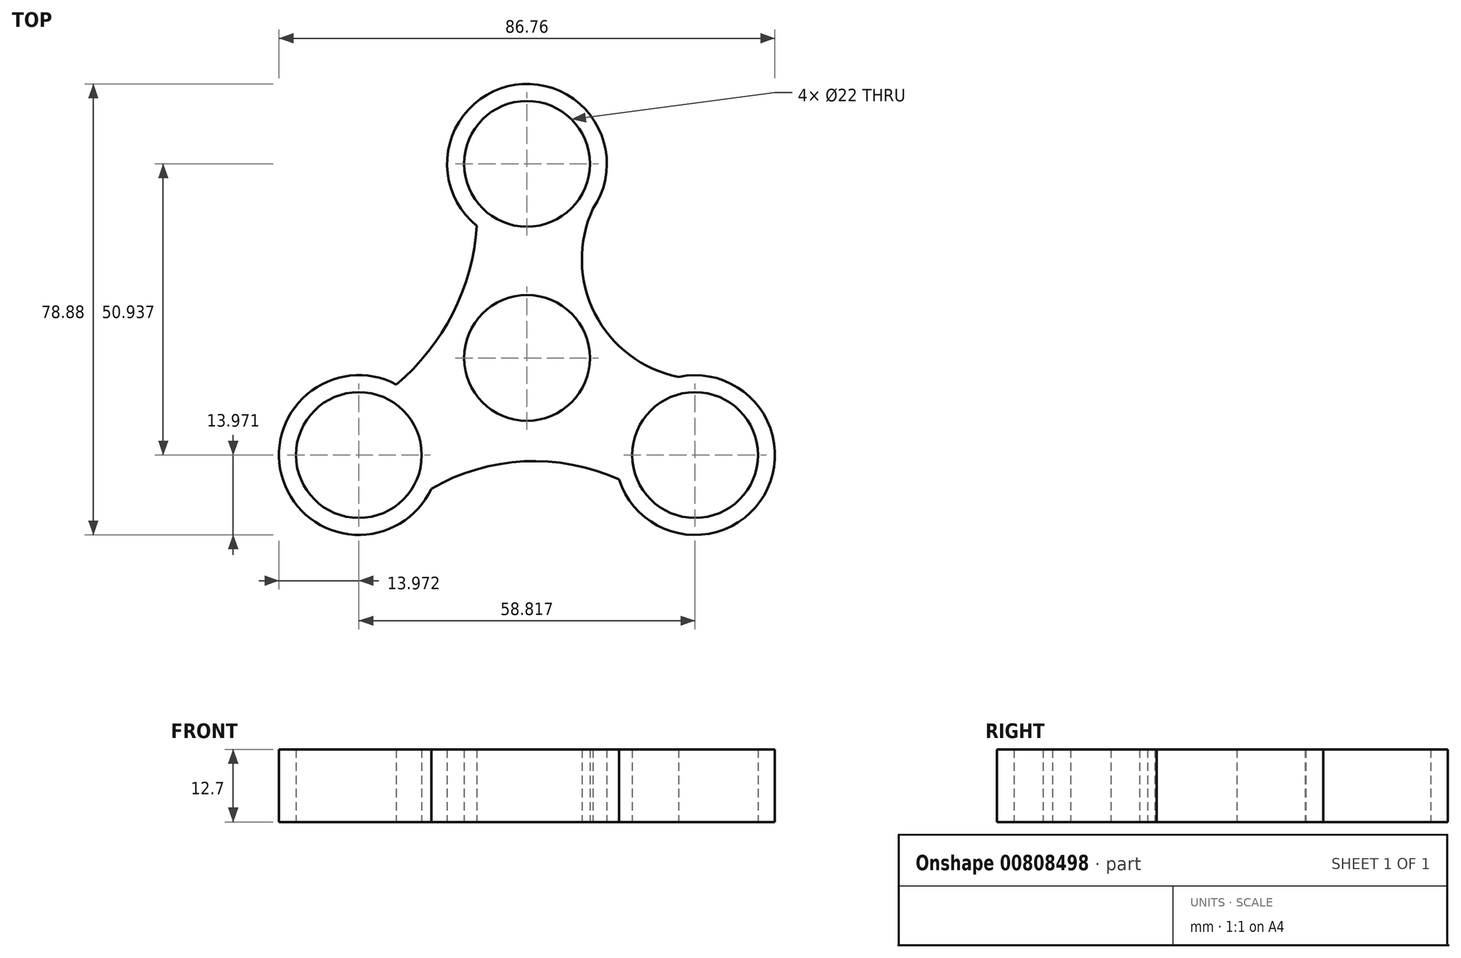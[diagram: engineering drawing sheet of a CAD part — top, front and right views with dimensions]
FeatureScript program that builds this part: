
annotation { "Feature Type Name" : "Feature", "Feature Type Description" : "" }
export const myFeature = defineFeature(function(context is Context, id is Id, definition is map)
    precondition{}
    {
        {
            var Q0;
            Q0=qCreatedBy(makeId("Top.planeOp"),FACE);
            var sketch = newSketch(context, id + "F0", { "sketchPlane" : qUnion([Q0])});
            skCircle(sketch, "E0", {"center": v(0, 0) * mm, "radius": 44.45 * mm});
            skCircle(sketch, "E1", {"center": v(0, 0) * mm, "radius": 11 * mm});
            skCircle(sketch, "E2", {"center": v(0, 33.96) * mm, "radius": 11 * mm});
            skCircle(sketch, "E3.1.0", {"center": v(-29.4, -16.98) * mm, "radius": 11 * mm});
            skCircle(sketch, "E3.2.0", {"center": v(29.4, -16.98) * mm, "radius": 11 * mm});
            skCircle(sketch, "E4", {"center": v(-29.4, -16.98) * mm, "radius": 13.97 * mm});
            skCircle(sketch, "E5", {"center": v(29.4, -16.98) * mm, "radius": 13.97 * mm});
            skCircle(sketch, "E6", {"center": v(0, 33.96) * mm, "radius": 13.97 * mm});
            skCircle(sketch, "E7", {"center": v(0, 0) * mm, "radius": 13.97 * mm});
            skArc(sketch, "E8", {"start": v(-22.87, -4.64) * mm, "mid": v(-12.97, 7.78) * mm, "end": v(-8.78, 23.1) * mm});
            skArc(sketch, "E9", {"start": v(11.57, 26.12) * mm, "mid": v(11.89, 7.77) * mm, "end": v(26.53, -3.3) * mm});
            skArc(sketch, "E10", {"start": v(16.1, -21.24) * mm, "mid": v(-0.51, -18.09) * mm, "end": v(-16.74, -22.86) * mm});
            skSolve(sketch);
        }
        {
            var Q0;
            Q0=makeQuery(id+"F0.imprint","IMPRINT",FACE,{"disambiguationData":[TD([[makeQuery(id+"F0.imprint","IMPRINT",EDGE,{"derivedFrom":sQuery(id+"F0.wireOp",EDGE,"E7")}),-1.0]])]});
            var Q1;
            {var subQ1=sQuery(id+"F0.wireOp",EDGE,"E0");var subQ4=sQuery(id+"F0.wireOp",EDGE,"E4");var subQ7=makeQuery(id+"F0.imprint","INTERSECT",VERTEX,{"disambiguationData":[OD(0.0)],"derivedFrom":[subQ1,subQ4]});Q1=makeQuery(id+"F0.imprint","IMPRINT",FACE,{"disambiguationData":[TD([[makeQuery(id+"F0.imprint","IMPRINT",EDGE,{"disambiguationData":[TD([[subQ7,-1.0]])],"derivedFrom":subQ1}),1.0]])]});}
            var Q2;
            {var subQ0=sQuery(id+"F0.wireOp",EDGE,"E6");var subQ2=sQuery(id+"F0.wireOp",EDGE,"E0");var subQ7=makeQuery(id+"F0.imprint","INTERSECT",VERTEX,{"disambiguationData":[OD(0.0)],"derivedFrom":[subQ2,subQ0]});Q2=makeQuery(id+"F0.imprint","IMPRINT",FACE,{"disambiguationData":[TD([[makeQuery(id+"F0.imprint","IMPRINT",EDGE,{"disambiguationData":[TD([[subQ7,-1.0]])],"derivedFrom":subQ2}),1.0]])]});}
            var Q3;
            {var subQ0=sQuery(id+"F0.wireOp",EDGE,"E4");var subQ1=sQuery(id+"F0.wireOp",EDGE,"E0");var subQ2=makeQuery(id+"F0.imprint","INTERSECT",VERTEX,{"disambiguationData":[OD(0.0)],"derivedFrom":[subQ1,subQ0]});Q3=makeQuery(id+"F0.imprint","IMPRINT",FACE,{"disambiguationData":[TD([[makeQuery(id+"F0.imprint","IMPRINT",EDGE,{"disambiguationData":[TD([[subQ2,-1.0]])],"derivedFrom":subQ1}),-1.0]])]});}
            var Q4;
            {var subQ0=sQuery(id+"F0.wireOp",EDGE,"E6");var subQ1=sQuery(id+"F0.wireOp",EDGE,"E0");var subQ2=makeQuery(id+"F0.imprint","INTERSECT",VERTEX,{"disambiguationData":[OD(0.0)],"derivedFrom":[subQ1,subQ0]});Q4=makeQuery(id+"F0.imprint","IMPRINT",FACE,{"disambiguationData":[TD([[makeQuery(id+"F0.imprint","IMPRINT",EDGE,{"disambiguationData":[TD([[subQ2,-1.0]])],"derivedFrom":subQ1}),-1.0]])]});}
            var Q5;
            {var subQ0=sQuery(id+"F0.wireOp",EDGE,"E5");var subQ1=sQuery(id+"F0.wireOp",EDGE,"E0");var subQ2=makeQuery(id+"F0.imprint","INTERSECT",VERTEX,{"disambiguationData":[OD(0.0)],"derivedFrom":[subQ1,subQ0]});Q5=makeQuery(id+"F0.imprint","IMPRINT",FACE,{"disambiguationData":[TD([[makeQuery(id+"F0.imprint","IMPRINT",EDGE,{"disambiguationData":[TD([[subQ2,-1.0]])],"derivedFrom":subQ1}),-1.0]])]});}
            var Q6;
            {var subQ0=sQuery(id+"F0.wireOp",EDGE,"E5");var subQ1=sQuery(id+"F0.wireOp",EDGE,"E0");var subQ7=makeQuery(id+"F0.imprint","INTERSECT",VERTEX,{"disambiguationData":[OD(0.0)],"derivedFrom":[subQ1,subQ0]});Q6=makeQuery(id+"F0.imprint","IMPRINT",FACE,{"disambiguationData":[TD([[makeQuery(id+"F0.imprint","IMPRINT",EDGE,{"disambiguationData":[TD([[subQ7,-1.0]])],"derivedFrom":subQ1}),1.0]])]});}
            var Q7;
            Q7=makeQuery(id+"F0.imprint","IMPRINT",FACE,{"disambiguationData":[TD([[makeQuery(id+"F0.imprint","IMPRINT",EDGE,{"derivedFrom":sQuery(id+"F0.wireOp",EDGE,"E1")}),-1.0]])]});
            extrude(context, id + "F1", {"entities" : qUnion([Q0, Q1, Q2, Q3, Q4, Q5, Q6, Q7]), "depth" : 12.7 * mm, "offsetDistance" : 25.4 * mm});
        }
    });
